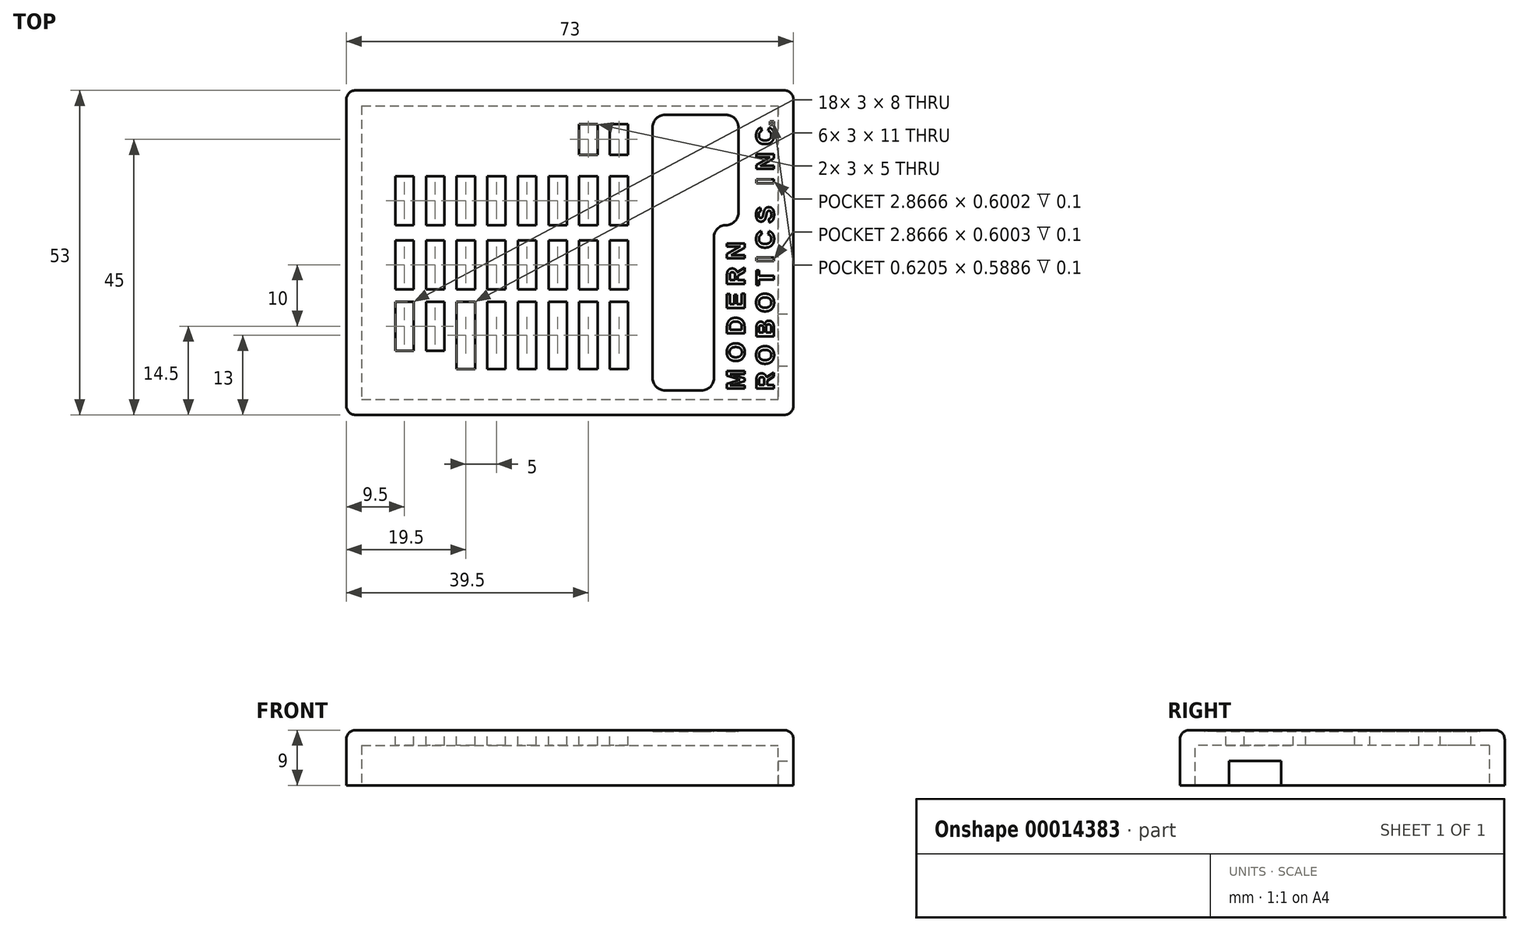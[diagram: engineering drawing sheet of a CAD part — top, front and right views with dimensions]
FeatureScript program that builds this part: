
annotation { "Feature Type Name" : "Feature", "Feature Type Description" : "" }
export const myFeature = defineFeature(function(context is Context, id is Id, definition is map)
    precondition{}
    {
        {
            var Q0;
            Q0=qCreatedBy(makeId("Top.planeOp"),FACE);
            var sketch = newSketch(context, id + "F0", { "sketchPlane" : qUnion([Q0])});
            skLineSegment(sketch, "E0.bottom", {"start": v(0, 0) * mm, "end": v(73, 0) * mm});
            skLineSegment(sketch, "E0.top", {"start": v(0, 53) * mm, "end": v(73, 53) * mm});
            skLineSegment(sketch, "E0.left", {"start": v(0, 0) * mm, "end": v(0, 53) * mm});
            skLineSegment(sketch, "E0.right", {"start": v(73, 0) * mm, "end": v(73, 53) * mm});
            skSolve(sketch);
        }
        {
            var Q0;
            Q0=qSketchRegion(id+"F0",true);
            extrude(context, id + "F1", {"entities" : qUnion([Q0]), "depth" : 9 * mm});
        }
        {
            var Q0;
            Q0=makeQuery(id+"F1.opExtrude","SWEPT_EDGE",EDGE,{"disambiguationData":[OSD([sQuery(id+"F0.wireOp",EDGE,"E0.bottom"),sQuery(id+"F0.wireOp",EDGE,"E0.left")])]});
            var Q1;
            Q1=makeQuery(id+"F1.opExtrude","CAP_EDGE",EDGE,{"disambiguationData":[OSD([sQuery(id+"F0.wireOp",EDGE,"E0.bottom")])],"isStart":false});
            var Q2;
            Q2=makeQuery(id+"F1.opExtrude","CAP_EDGE",EDGE,{"disambiguationData":[OSD([sQuery(id+"F0.wireOp",EDGE,"E0.left")])],"isStart":false});
            var Q3;
            Q3=makeQuery(id+"F1.opExtrude","SWEPT_EDGE",EDGE,{"disambiguationData":[OSD([sQuery(id+"F0.wireOp",EDGE,"E0.bottom"),sQuery(id+"F0.wireOp",EDGE,"E0.right")])]});
            var Q4;
            Q4=makeQuery(id+"F1.opExtrude","CAP_EDGE",EDGE,{"disambiguationData":[OSD([sQuery(id+"F0.wireOp",EDGE,"E0.right")])],"isStart":false});
            var Q5;
            Q5=makeQuery(id+"F1.opExtrude","CAP_EDGE",EDGE,{"disambiguationData":[OSD([sQuery(id+"F0.wireOp",EDGE,"E0.top")])],"isStart":false});
            var Q6;
            Q6=makeQuery(id+"F1.opExtrude","SWEPT_EDGE",EDGE,{"disambiguationData":[OSD([sQuery(id+"F0.wireOp",EDGE,"E0.top"),sQuery(id+"F0.wireOp",EDGE,"E0.right")])]});
            var Q7;
            Q7=makeQuery(id+"F1.opExtrude","SWEPT_EDGE",EDGE,{"disambiguationData":[OSD([sQuery(id+"F0.wireOp",EDGE,"E0.top"),sQuery(id+"F0.wireOp",EDGE,"E0.left")])]});
            fillet(context, id + "F2", {"entities" : qUnion([Q0, Q1, Q2, Q3, Q4, Q5, Q6, Q7]), "radius" : 1.5 * mm, "tangentPropagation" : true, "allowEdgeOverflow" : false});
        }
        {
            var Q0;
            Q0=makeQuery(id+"F1.opExtrude","CAP_FACE",FACE,{"disambiguationData":[OSD([sQuery(id+"F0.wireOp",EDGE,"E0.bottom"),sQuery(id+"F0.wireOp",EDGE,"E0.top"),sQuery(id+"F0.wireOp",EDGE,"E0.left"),sQuery(id+"F0.wireOp",EDGE,"E0.right")])],"isStart":true});
            shell(context, id + "F3", {"entities" : qUnion([Q0]), "thickness" : 2.5 * mm});
        }
        {
            var Q0;
            Q0=makeQuery(id+"F1.opExtrude","SWEPT_FACE",FACE,{"disambiguationData":[OSD([sQuery(id+"F0.wireOp",EDGE,"E0.right")])]});
            var sketch = newSketch(context, id + "F4", { "sketchPlane" : qUnion([Q0])});
            skLineSegment(sketch, "E1.bottom", {"start": v(8, 4) * mm, "end": v(16.5, 4) * mm});
            skLineSegment(sketch, "E1.top", {"start": v(8, 0) * mm, "end": v(16.5, 0) * mm});
            skLineSegment(sketch, "E1.left", {"start": v(8, 4) * mm, "end": v(8, 0) * mm});
            skLineSegment(sketch, "E1.right", {"start": v(16.5, 4) * mm, "end": v(16.5, 0) * mm});
            skPoint(sketch, "E2", {"position": v(16.97, -0.37) * mm});
            skPoint(sketch, "E3", {"position": v(100.9, 31.9) * mm});
            skSolve(sketch);
        }
        {
            var Q0;
            Q0=qSketchRegion(id+"F4",true);
            extrude(context, id + "F5", {"entities" : qUnion([Q0]), "operationType" : NewBodyOperationType.REMOVE, "endBound" : BoundingType.UP_TO_NEXT, "oppositeDirection" : true, "depth" : 25 * mm});
        }
        {
            var Q0;
            Q0=makeQuery(id+"F1.opExtrude","CAP_FACE",FACE,{"disambiguationData":[OSD([sQuery(id+"F0.wireOp",EDGE,"E0.bottom"),sQuery(id+"F0.wireOp",EDGE,"E0.top"),sQuery(id+"F0.wireOp",EDGE,"E0.left"),sQuery(id+"F0.wireOp",EDGE,"E0.right")])],"isStart":false});
            var sketch = newSketch(context, id + "F6", { "sketchPlane" : qUnion([Q0])});
            skText(sketch, "E4", { "text": "M O D E R N\nR O B O T I C S   I N C.", "fontName": "Arimo-Bold.ttf"});
            const initialGuessF6  = {"E4": [0.065, 0.004, 0, 1, 0.003]};
            skSetInitialGuess(sketch, initialGuessF6);
            skSolve(sketch);
        }
        {
            var Q0;
            Q0=qSketchRegion(id+"F6",true);
            extrude(context, id + "F7", {"entities" : qUnion([Q0]), "operationType" : NewBodyOperationType.REMOVE, "oppositeDirection" : true, "depth" : .1 * mm});
        }
        {
            var Q0;
            Q0=makeQuery(id+"F6.imprint","IMPRINT",FACE,{"disambiguationData":[TD([[makeQuery(id+"F6.imprint","IMPRINT",EDGE,{"derivedFrom":sQuery(id+"F6.wireOp",EDGE,"E4.sketch_text.stroke-0")}),1.0]])]});
            var sketch = newSketch(context, id + "F8", { "sketchPlane" : qUnion([Q0])});
            skLineSegment(sketch, "E5.bottom", {"start": v(8, 31) * mm, "end": v(11, 31) * mm});
            skLineSegment(sketch, "E5.top", {"start": v(8, 39) * mm, "end": v(11, 39) * mm});
            skLineSegment(sketch, "E5.left", {"start": v(8, 31) * mm, "end": v(8, 39) * mm});
            skLineSegment(sketch, "E5.right", {"start": v(11, 31) * mm, "end": v(11, 39) * mm});
            skLineSegment(sketch, "E6.0.1.0", {"start": v(8, 20.5) * mm, "end": v(8, 28.5) * mm});
            skLineSegment(sketch, "E6.0.1.1", {"start": v(11, 20.5) * mm, "end": v(11, 28.5) * mm});
            skLineSegment(sketch, "E6.0.1.2", {"start": v(8, 20.5) * mm, "end": v(11, 20.5) * mm});
            skLineSegment(sketch, "E6.0.1.3", {"start": v(8, 28.5) * mm, "end": v(11, 28.5) * mm});
            skLineSegment(sketch, "E6.1.0.0", {"start": v(13, 31) * mm, "end": v(13, 39) * mm});
            skLineSegment(sketch, "E6.1.0.1", {"start": v(16, 31) * mm, "end": v(16, 39) * mm});
            skLineSegment(sketch, "E6.1.0.2", {"start": v(13, 31) * mm, "end": v(16, 31) * mm});
            skLineSegment(sketch, "E6.1.0.3", {"start": v(13, 39) * mm, "end": v(16, 39) * mm});
            skLineSegment(sketch, "E6.1.1.0", {"start": v(13, 20.5) * mm, "end": v(13, 28.5) * mm});
            skLineSegment(sketch, "E6.1.1.1", {"start": v(16, 20.5) * mm, "end": v(16, 28.5) * mm});
            skLineSegment(sketch, "E6.1.1.2", {"start": v(13, 20.5) * mm, "end": v(16, 20.5) * mm});
            skLineSegment(sketch, "E6.1.1.3", {"start": v(13, 28.5) * mm, "end": v(16, 28.5) * mm});
            skLineSegment(sketch, "E6.2.0.0", {"start": v(18, 31) * mm, "end": v(18, 39) * mm});
            skLineSegment(sketch, "E6.2.0.1", {"start": v(21, 31) * mm, "end": v(21, 39) * mm});
            skLineSegment(sketch, "E6.2.0.2", {"start": v(18, 31) * mm, "end": v(21, 31) * mm});
            skLineSegment(sketch, "E6.2.0.3", {"start": v(18, 39) * mm, "end": v(21, 39) * mm});
            skLineSegment(sketch, "E6.2.1.0", {"start": v(18, 20.5) * mm, "end": v(18, 28.5) * mm});
            skLineSegment(sketch, "E6.2.1.1", {"start": v(21, 20.5) * mm, "end": v(21, 28.5) * mm});
            skLineSegment(sketch, "E6.2.1.2", {"start": v(18, 20.5) * mm, "end": v(21, 20.5) * mm});
            skLineSegment(sketch, "E6.2.1.3", {"start": v(18, 28.5) * mm, "end": v(21, 28.5) * mm});
            skLineSegment(sketch, "E6.3.0.0", {"start": v(23, 31) * mm, "end": v(23, 39) * mm});
            skLineSegment(sketch, "E6.3.0.1", {"start": v(26, 31) * mm, "end": v(26, 39) * mm});
            skLineSegment(sketch, "E6.3.0.2", {"start": v(23, 31) * mm, "end": v(26, 31) * mm});
            skLineSegment(sketch, "E6.3.0.3", {"start": v(23, 39) * mm, "end": v(26, 39) * mm});
            skLineSegment(sketch, "E6.3.1.0", {"start": v(23, 20.5) * mm, "end": v(23, 28.5) * mm});
            skLineSegment(sketch, "E6.3.1.1", {"start": v(26, 20.5) * mm, "end": v(26, 28.5) * mm});
            skLineSegment(sketch, "E6.3.1.2", {"start": v(23, 20.5) * mm, "end": v(26, 20.5) * mm});
            skLineSegment(sketch, "E6.3.1.3", {"start": v(23, 28.5) * mm, "end": v(26, 28.5) * mm});
            skLineSegment(sketch, "E6.4.0.0", {"start": v(28, 31) * mm, "end": v(28, 39) * mm});
            skLineSegment(sketch, "E6.4.0.1", {"start": v(31, 31) * mm, "end": v(31, 39) * mm});
            skLineSegment(sketch, "E6.4.0.2", {"start": v(28, 31) * mm, "end": v(31, 31) * mm});
            skLineSegment(sketch, "E6.4.0.3", {"start": v(28, 39) * mm, "end": v(31, 39) * mm});
            skLineSegment(sketch, "E6.4.1.0", {"start": v(28, 20.5) * mm, "end": v(28, 28.5) * mm});
            skLineSegment(sketch, "E6.4.1.1", {"start": v(31, 20.5) * mm, "end": v(31, 28.5) * mm});
            skLineSegment(sketch, "E6.4.1.2", {"start": v(28, 20.5) * mm, "end": v(31, 20.5) * mm});
            skLineSegment(sketch, "E6.4.1.3", {"start": v(28, 28.5) * mm, "end": v(31, 28.5) * mm});
            skLineSegment(sketch, "E6.5.0.0", {"start": v(33, 31) * mm, "end": v(33, 39) * mm});
            skLineSegment(sketch, "E6.5.0.1", {"start": v(36, 31) * mm, "end": v(36, 39) * mm});
            skLineSegment(sketch, "E6.5.0.2", {"start": v(33, 31) * mm, "end": v(36, 31) * mm});
            skLineSegment(sketch, "E6.5.0.3", {"start": v(33, 39) * mm, "end": v(36, 39) * mm});
            skLineSegment(sketch, "E6.5.1.0", {"start": v(33, 20.5) * mm, "end": v(33, 28.5) * mm});
            skLineSegment(sketch, "E6.5.1.1", {"start": v(36, 20.5) * mm, "end": v(36, 28.5) * mm});
            skLineSegment(sketch, "E6.5.1.2", {"start": v(33, 20.5) * mm, "end": v(36, 20.5) * mm});
            skLineSegment(sketch, "E6.5.1.3", {"start": v(33, 28.5) * mm, "end": v(36, 28.5) * mm});
            skLineSegment(sketch, "E6.6.0.0", {"start": v(38, 31) * mm, "end": v(38, 39) * mm});
            skLineSegment(sketch, "E6.6.0.1", {"start": v(41, 31) * mm, "end": v(41, 39) * mm});
            skLineSegment(sketch, "E6.6.0.2", {"start": v(38, 31) * mm, "end": v(41, 31) * mm});
            skLineSegment(sketch, "E6.6.0.3", {"start": v(38, 39) * mm, "end": v(41, 39) * mm});
            skLineSegment(sketch, "E6.6.1.0", {"start": v(38, 20.5) * mm, "end": v(38, 28.5) * mm});
            skLineSegment(sketch, "E6.6.1.1", {"start": v(41, 20.5) * mm, "end": v(41, 28.5) * mm});
            skLineSegment(sketch, "E6.6.1.2", {"start": v(38, 20.5) * mm, "end": v(41, 20.5) * mm});
            skLineSegment(sketch, "E6.6.1.3", {"start": v(38, 28.5) * mm, "end": v(41, 28.5) * mm});
            skLineSegment(sketch, "E6.7.0.0", {"start": v(43, 31) * mm, "end": v(43, 39) * mm});
            skLineSegment(sketch, "E6.7.0.1", {"start": v(46, 31) * mm, "end": v(46, 39) * mm});
            skLineSegment(sketch, "E6.7.0.2", {"start": v(43, 31) * mm, "end": v(46, 31) * mm});
            skLineSegment(sketch, "E6.7.0.3", {"start": v(43, 39) * mm, "end": v(46, 39) * mm});
            skLineSegment(sketch, "E6.7.1.0", {"start": v(43, 20.5) * mm, "end": v(43, 28.5) * mm});
            skLineSegment(sketch, "E6.7.1.1", {"start": v(46, 20.5) * mm, "end": v(46, 28.5) * mm});
            skLineSegment(sketch, "E6.7.1.2", {"start": v(43, 20.5) * mm, "end": v(46, 20.5) * mm});
            skLineSegment(sketch, "E6.7.1.3", {"start": v(43, 28.5) * mm, "end": v(46, 28.5) * mm});
            skLineSegment(sketch, "E6.direction1", {"start": v(8, 31) * mm, "end": v(13, 31) * mm, "construction": true});
            skLineSegment(sketch, "E6.direction2", {"start": v(8, 31) * mm, "end": v(8, 20.5) * mm, "construction": true});
            skLineSegment(sketch, "E7.0.1.0", {"start": v(13, 10.5) * mm, "end": v(13, 18.5) * mm});
            skLineSegment(sketch, "E7.0.1.1", {"start": v(13, 18.5) * mm, "end": v(16, 18.5) * mm});
            skLineSegment(sketch, "E7.0.1.2", {"start": v(16, 10.5) * mm, "end": v(16, 18.5) * mm});
            skLineSegment(sketch, "E7.0.1.3", {"start": v(13, 10.5) * mm, "end": v(16, 10.5) * mm});
            skLineSegment(sketch, "E7.0.1.4", {"start": v(8, 10.5) * mm, "end": v(11, 10.5) * mm});
            skLineSegment(sketch, "E7.0.1.5", {"start": v(8, 18.5) * mm, "end": v(11, 18.5) * mm});
            skLineSegment(sketch, "E7.0.1.6", {"start": v(8, 10.5) * mm, "end": v(8, 18.5) * mm});
            skLineSegment(sketch, "E7.0.1.7", {"start": v(11, 10.5) * mm, "end": v(11, 18.5) * mm});
            skLineSegment(sketch, "E7.0.1.8", {"start": v(8, 21) * mm, "end": v(8, 10.5) * mm, "construction": true});
            skLineSegment(sketch, "E7.direction1", {"start": v(13, 20.5) * mm, "end": v(15.38, 20.5) * mm, "construction": true});
            skLineSegment(sketch, "E7.direction2", {"start": v(13, 20.5) * mm, "end": v(13, 10.5) * mm, "construction": true});
            skLineSegment(sketch, "E8.bottom", {"start": v(18, 18.5) * mm, "end": v(21, 18.5) * mm});
            skLineSegment(sketch, "E8.top", {"start": v(18, 7.5) * mm, "end": v(21, 7.5) * mm});
            skLineSegment(sketch, "E8.left", {"start": v(18, 18.5) * mm, "end": v(18, 7.5) * mm});
            skLineSegment(sketch, "E8.right", {"start": v(21, 18.5) * mm, "end": v(21, 7.5) * mm});
            skLineSegment(sketch, "E9.1.0.0", {"start": v(26, 18.5) * mm, "end": v(26, 7.5) * mm});
            skLineSegment(sketch, "E9.1.0.1", {"start": v(23, 18.5) * mm, "end": v(23, 7.5) * mm});
            skLineSegment(sketch, "E9.1.0.2", {"start": v(23, 7.5) * mm, "end": v(26, 7.5) * mm});
            skLineSegment(sketch, "E9.1.0.3", {"start": v(23, 18.5) * mm, "end": v(26, 18.5) * mm});
            skLineSegment(sketch, "E9.2.0.0", {"start": v(31, 18.5) * mm, "end": v(31, 7.5) * mm});
            skLineSegment(sketch, "E9.2.0.1", {"start": v(28, 18.5) * mm, "end": v(28, 7.5) * mm});
            skLineSegment(sketch, "E9.2.0.2", {"start": v(28, 7.5) * mm, "end": v(31, 7.5) * mm});
            skLineSegment(sketch, "E9.2.0.3", {"start": v(28, 18.5) * mm, "end": v(31, 18.5) * mm});
            skLineSegment(sketch, "E9.3.0.0", {"start": v(36, 18.5) * mm, "end": v(36, 7.5) * mm});
            skLineSegment(sketch, "E9.3.0.1", {"start": v(33, 18.5) * mm, "end": v(33, 7.5) * mm});
            skLineSegment(sketch, "E9.3.0.2", {"start": v(33, 7.5) * mm, "end": v(36, 7.5) * mm});
            skLineSegment(sketch, "E9.3.0.3", {"start": v(33, 18.5) * mm, "end": v(36, 18.5) * mm});
            skLineSegment(sketch, "E9.4.0.0", {"start": v(41, 18.5) * mm, "end": v(41, 7.5) * mm});
            skLineSegment(sketch, "E9.4.0.1", {"start": v(38, 18.5) * mm, "end": v(38, 7.5) * mm});
            skLineSegment(sketch, "E9.4.0.2", {"start": v(38, 7.5) * mm, "end": v(41, 7.5) * mm});
            skLineSegment(sketch, "E9.4.0.3", {"start": v(38, 18.5) * mm, "end": v(41, 18.5) * mm});
            skLineSegment(sketch, "E9.5.0.0", {"start": v(46, 18.5) * mm, "end": v(46, 7.5) * mm});
            skLineSegment(sketch, "E9.5.0.1", {"start": v(43, 18.5) * mm, "end": v(43, 7.5) * mm});
            skLineSegment(sketch, "E9.5.0.2", {"start": v(43, 7.5) * mm, "end": v(46, 7.5) * mm});
            skLineSegment(sketch, "E9.5.0.3", {"start": v(43, 18.5) * mm, "end": v(46, 18.5) * mm});
            skLineSegment(sketch, "E9.direction1", {"start": v(21, 7.5) * mm, "end": v(26, 7.5) * mm, "construction": true});
            skLineSegment(sketch, "E10.bottom", {"start": v(46, 42.5) * mm, "end": v(43, 42.5) * mm});
            skLineSegment(sketch, "E10.top", {"start": v(46, 47.5) * mm, "end": v(43, 47.5) * mm});
            skLineSegment(sketch, "E10.left", {"start": v(46, 42.5) * mm, "end": v(46, 47.5) * mm});
            skLineSegment(sketch, "E10.right", {"start": v(43, 42.5) * mm, "end": v(43, 47.5) * mm});
            skLineSegment(sketch, "E11.1.0.0", {"start": v(41, 42.5) * mm, "end": v(38, 42.5) * mm});
            skLineSegment(sketch, "E11.1.0.1", {"start": v(41, 42.5) * mm, "end": v(41, 47.5) * mm});
            skLineSegment(sketch, "E11.1.0.2", {"start": v(38, 42.5) * mm, "end": v(38, 47.5) * mm});
            skLineSegment(sketch, "E11.1.0.3", {"start": v(41, 47.5) * mm, "end": v(38, 47.5) * mm});
            skLineSegment(sketch, "E11.direction1", {"start": v(43, 42.5) * mm, "end": v(38, 42.5) * mm, "construction": true});
            skSolve(sketch);
        }
        {
            var Q0;
            Q0=qSketchRegion(id+"F8",true);
            extrude(context, id + "F9", {"entities" : qUnion([Q0]), "operationType" : NewBodyOperationType.REMOVE, "endBound" : BoundingType.UP_TO_NEXT, "oppositeDirection" : true, "depth" : 25 * mm});
        }
        {
            var Q0;
            {var subQ0=sQuery(id+"F0.wireOp",EDGE,"E0.bottom");var subQ1=sQuery(id+"F0.wireOp",EDGE,"E0.top");var subQ2=sQuery(id+"F0.wireOp",EDGE,"E0.left");var subQ3=sQuery(id+"F0.wireOp",EDGE,"E0.right");Q0=makeQuery(id+"F7.boolean.opBoolean","SPLIT",FACE,{"disambiguationData":[TD([makeQuery(id+"F2.opFillet","BLEND_FACE",FACE,{"disambiguationData":[OSD([subQ0])]})])],"derivedFrom":makeQuery(id+"F1.opExtrude","CAP_FACE",FACE,{"disambiguationData":[OSD([subQ0,subQ1,subQ2,subQ3])],"isStart":false})});}
            var sketch = newSketch(context, id + "F10", { "sketchPlane" : qUnion([Q0])});
            skLineSegment(sketch, "E12.bottom", {"start": v(52, 4) * mm, "end": v(58, 4) * mm});
            skLineSegment(sketch, "E12.left", {"start": v(50, 6) * mm, "end": v(50, 47) * mm});
            skLineSegment(sketch, "E12.right", {"start": v(60, 6) * mm, "end": v(60, 29) * mm});
            skLineSegment(sketch, "E13.top", {"start": v(62, 31) * mm, "end": v(62, 31) * mm});
            skLineSegment(sketch, "E14", {"start": v(64, 33) * mm, "end": v(64, 47) * mm});
            skLineSegment(sketch, "E15", {"start": v(62, 49) * mm, "end": v(52, 49) * mm});
            skPoint(sketch, "E16.visualSharp", {"position": v(50, 4) * mm});
            skArc(sketch, "E16.filletArc", {"start": v(50, 6) * mm, "mid": v(50.59, 4.59) * mm, "end": v(52, 4) * mm});
            skPoint(sketch, "E17.visualSharp", {"position": v(60, 4) * mm});
            skArc(sketch, "E17.filletArc", {"start": v(58, 4) * mm, "mid": v(59.41, 4.59) * mm, "end": v(60, 6) * mm});
            skPoint(sketch, "E18.visualSharp", {"position": v(60, 31) * mm});
            skArc(sketch, "E18.filletArc", {"start": v(62, 31) * mm, "mid": v(60.59, 30.41) * mm, "end": v(60, 29) * mm});
            skPoint(sketch, "E19.visualSharp", {"position": v(64, 49) * mm});
            skArc(sketch, "E19.filletArc", {"start": v(64, 47) * mm, "mid": v(63.41, 48.41) * mm, "end": v(62, 49) * mm});
            skPoint(sketch, "E20.visualSharp", {"position": v(64, 31) * mm});
            skArc(sketch, "E20.filletArc", {"start": v(62, 31) * mm, "mid": v(63.41, 31.59) * mm, "end": v(64, 33) * mm});
            skPoint(sketch, "E21.newPointB", {"position": v(50, 49) * mm});
            skArc(sketch, "E21.filletArc", {"start": v(52, 49) * mm, "mid": v(50.59, 48.4) * mm, "end": v(50, 47) * mm});
            skSolve(sketch);
        }
        {
            var Q0;
            Q0=qSketchRegion(id+"F10",true);
            extrude(context, id + "F11", {"entities" : qUnion([Q0]), "operationType" : NewBodyOperationType.REMOVE, "oppositeDirection" : true, "depth" : .2 * mm});
        }
        {
            var Q0;
            Q0=makeQuery(id+"F11.boolean.opBoolean","COPY",FACE,{"derivedFrom":makeQuery(id+"F11.opExtrude","CAP_FACE",FACE,{"disambiguationData":[OSD([sQuery(id+"F10.wireOp",EDGE,"E12.bottom"),sQuery(id+"F10.wireOp",EDGE,"E12.left"),sQuery(id+"F10.wireOp",EDGE,"E12.right"),sQuery(id+"F10.wireOp",EDGE,"E14"),sQuery(id+"F10.wireOp",EDGE,"E15"),sQuery(id+"F10.wireOp",EDGE,"E16.filletArc"),sQuery(id+"F10.wireOp",EDGE,"E17.filletArc"),sQuery(id+"F10.wireOp",EDGE,"E18.filletArc"),sQuery(id+"F10.wireOp",EDGE,"E19.filletArc"),sQuery(id+"F10.wireOp",EDGE,"E20.filletArc"),sQuery(id+"F10.wireOp",EDGE,"E21.filletArc")])],"isStart":false})});
            var Q1;
            Q1=makeQuery(id+"F11.boolean.opBoolean","COPY",EDGE,{"derivedFrom":makeQuery(id+"F11.opExtrude","CAP_EDGE",EDGE,{"disambiguationData":[OSD([sQuery(id+"F10.wireOp",EDGE,"E12.left")])],"isStart":true})});
            var Q2;
            Q2=makeQuery(id+"F11.boolean.opBoolean","COPY",EDGE,{"derivedFrom":makeQuery(id+"F11.opExtrude","CAP_EDGE",EDGE,{"disambiguationData":[OSD([sQuery(id+"F10.wireOp",EDGE,"E19.filletArc")])],"isStart":true})});
            var Q3;
            Q3=makeQuery(id+"F11.boolean.opBoolean","COPY",EDGE,{"derivedFrom":makeQuery(id+"F11.opExtrude","CAP_EDGE",EDGE,{"disambiguationData":[OSD([sQuery(id+"F10.wireOp",EDGE,"E21.filletArc")])],"isStart":true})});
            var Q4;
            Q4=makeQuery(id+"F11.boolean.opBoolean","COPY",EDGE,{"derivedFrom":makeQuery(id+"F11.opExtrude","CAP_EDGE",EDGE,{"disambiguationData":[OSD([sQuery(id+"F10.wireOp",EDGE,"E15")])],"isStart":true})});
            var Q5;
            Q5=makeQuery(id+"F11.boolean.opBoolean","COPY",EDGE,{"derivedFrom":makeQuery(id+"F11.opExtrude","CAP_EDGE",EDGE,{"disambiguationData":[OSD([sQuery(id+"F10.wireOp",EDGE,"E21.filletArc")])],"isStart":false})});
            var Q6;
            Q6=makeQuery(id+"F11.boolean.opBoolean","COPY",EDGE,{"derivedFrom":makeQuery(id+"F11.opExtrude","CAP_EDGE",EDGE,{"disambiguationData":[OSD([sQuery(id+"F10.wireOp",EDGE,"E19.filletArc")])],"isStart":false})});
            var Q7;
            Q7=makeQuery(id+"F11.boolean.opBoolean","COPY",EDGE,{"derivedFrom":makeQuery(id+"F11.opExtrude","CAP_EDGE",EDGE,{"disambiguationData":[OSD([sQuery(id+"F10.wireOp",EDGE,"E15")])],"isStart":false})});
            var Q8;
            Q8=makeQuery(id+"F11.boolean.opBoolean","COPY",EDGE,{"derivedFrom":makeQuery(id+"F11.opExtrude","CAP_EDGE",EDGE,{"disambiguationData":[OSD([sQuery(id+"F10.wireOp",EDGE,"E20.filletArc")])],"isStart":true})});
            var Q9;
            Q9=makeQuery(id+"F11.boolean.opBoolean","COPY",EDGE,{"derivedFrom":makeQuery(id+"F11.opExtrude","CAP_EDGE",EDGE,{"disambiguationData":[OSD([sQuery(id+"F10.wireOp",EDGE,"E14")])],"isStart":true})});
            var Q10;
            Q10=makeQuery(id+"F11.boolean.opBoolean","COPY",EDGE,{"derivedFrom":makeQuery(id+"F11.opExtrude","CAP_EDGE",EDGE,{"disambiguationData":[OSD([sQuery(id+"F10.wireOp",EDGE,"E20.filletArc")])],"isStart":false})});
            var Q11;
            Q11=makeQuery(id+"F11.boolean.opBoolean","COPY",EDGE,{"derivedFrom":makeQuery(id+"F11.opExtrude","CAP_EDGE",EDGE,{"disambiguationData":[OSD([sQuery(id+"F10.wireOp",EDGE,"E14")])],"isStart":false})});
            var Q12;
            Q12=makeQuery(id+"F11.boolean.opBoolean","COPY",EDGE,{"derivedFrom":makeQuery(id+"F11.opExtrude","CAP_EDGE",EDGE,{"disambiguationData":[OSD([sQuery(id+"F10.wireOp",EDGE,"E18.filletArc")])],"isStart":true})});
            var Q13;
            Q13=makeQuery(id+"F11.boolean.opBoolean","COPY",EDGE,{"derivedFrom":makeQuery(id+"F11.opExtrude","CAP_EDGE",EDGE,{"disambiguationData":[OSD([sQuery(id+"F10.wireOp",EDGE,"E18.filletArc")])],"isStart":false})});
            var Q14;
            Q14=makeQuery(id+"F11.boolean.opBoolean","COPY",EDGE,{"derivedFrom":makeQuery(id+"F11.opExtrude","CAP_EDGE",EDGE,{"disambiguationData":[OSD([sQuery(id+"F10.wireOp",EDGE,"E12.right")])],"isStart":true})});
            var Q15;
            Q15=makeQuery(id+"F11.boolean.opBoolean","COPY",EDGE,{"derivedFrom":makeQuery(id+"F11.opExtrude","CAP_EDGE",EDGE,{"disambiguationData":[OSD([sQuery(id+"F10.wireOp",EDGE,"E12.right")])],"isStart":false})});
            var Q16;
            Q16=makeQuery(id+"F11.boolean.opBoolean","COPY",EDGE,{"derivedFrom":makeQuery(id+"F11.opExtrude","CAP_EDGE",EDGE,{"disambiguationData":[OSD([sQuery(id+"F10.wireOp",EDGE,"E16.filletArc")])],"isStart":true})});
            var Q17;
            Q17=makeQuery(id+"F11.boolean.opBoolean","COPY",EDGE,{"derivedFrom":makeQuery(id+"F11.opExtrude","CAP_EDGE",EDGE,{"disambiguationData":[OSD([sQuery(id+"F10.wireOp",EDGE,"E17.filletArc")])],"isStart":true})});
            var Q18;
            Q18=makeQuery(id+"F11.boolean.opBoolean","COPY",EDGE,{"derivedFrom":makeQuery(id+"F11.opExtrude","CAP_EDGE",EDGE,{"disambiguationData":[OSD([sQuery(id+"F10.wireOp",EDGE,"E12.bottom")])],"isStart":true})});
            var Q19;
            Q19=makeQuery(id+"F11.boolean.opBoolean","COPY",EDGE,{"derivedFrom":makeQuery(id+"F11.opExtrude","CAP_EDGE",EDGE,{"disambiguationData":[OSD([sQuery(id+"F10.wireOp",EDGE,"E12.bottom")])],"isStart":false})});
            var Q20;
            Q20=makeQuery(id+"F11.boolean.opBoolean","COPY",EDGE,{"derivedFrom":makeQuery(id+"F11.opExtrude","CAP_EDGE",EDGE,{"disambiguationData":[OSD([sQuery(id+"F10.wireOp",EDGE,"E16.filletArc")])],"isStart":false})});
            var Q21;
            Q21=makeQuery(id+"F11.boolean.opBoolean","COPY",EDGE,{"derivedFrom":makeQuery(id+"F11.opExtrude","CAP_EDGE",EDGE,{"disambiguationData":[OSD([sQuery(id+"F10.wireOp",EDGE,"E17.filletArc")])],"isStart":false})});
            fillet(context, id + "F12", {"entities" : qUnion([Q0, Q1, Q2, Q3, Q4, Q5, Q6, Q7, Q8, Q9, Q10, Q11, Q12, Q13, Q14, Q15, Q16, Q17, Q18, Q19, Q20, Q21]), "radius" : .1 * mm, "tangentPropagation" : true, "allowEdgeOverflow" : false});
        }
    });
